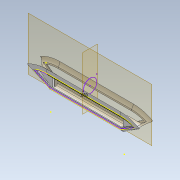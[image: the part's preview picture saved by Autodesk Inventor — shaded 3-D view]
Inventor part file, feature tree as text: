
AUTODESK INVENTOR PART (.ipt)
format: ipt  version: 2021 (Build 250183000, 183)  size: 614,912 bytes
history: native  units: in
note: dims shown in document units (in); Inventor stores cm internally (conversion verified against a paired STEP export)
features: sketch x11, extrude x7, move_body x4, plane x3, fillet x3, sweep x2, direct_edit x2, mirror x2, shell x1, projected_geometry x1
ambient origin geometry x8: Origin, YZ Plane, XZ Plane, XY Plane, X Axis, Y Axis, Z Axis, Center Point
bodies: Solid1 (feature_tree)
feature tree (36):
  extrude  "Extrusion1"  Depth=1.0in
  sweep  "Sweep1"
  direct_edit  "Direct Edit1"
  plane  "Work Plane1"
  plane  "Work Plane2"
  sweep  "Sweep2"
  fillet  "Fillet1"  [1 undecoded]
  fillet  "Fillet2"  Radius=2.75in
  fillet  "Fillet3"  [1 undecoded]
  shell  "Shell1"  Thickness=0.19in
  sketch  "Sketch4"  dims[d10=0.0in d11=0.0in d12=0.375in]
  extrude  "Extrusion2"  Depth=0.05in
  extrude  "Extrusion3"  Depth=0.05in TaperAngle=0.0deg
  plane  "Work Plane3"
  extrude  "Extrusion5"  Depth=0.7068in
  mirror  "Mirror2"
  extrude  "Extrusion6"  Depth=0.05in
  extrude  "Extrusion7"  Depth=0.7068in TaperAngle=0.0deg
  extrude  "Extrusion8"  Depth=0.31in TaperAngle=0.0deg
  mirror  "Mirror3"
  sketch  "Sketch10"  dims[d35=0.05in d36=0.0in d37=0.05in d38=0.0in d42=0.5in d43=0.05in d44=0.08in d45=0.0in d46=0.31in d47=0.0in d48=0.12in d49=0.7068in d50=0.0in d51=0.12in d52=0.035in d53=0.035in d54=0.7068in d55=0.0in d56=0.0in d57=0.0in d58=-0.07in d59=0.0in d60=0.0in d61=-0.07in]
  direct_edit  "Direct Edit2"
  sketch  "Sketch1"  dims[d0=5.5in d1=1.0in]
  sketch  "Sketch2"  dims[d3=1.0in d4=1.0in]
  sketch  "3D Sketch1"
  sketch  "Sketch3"  dims[d5=1.0in d6=0.0in d7=0.5in d8=0.0in d9=0.0in]
  sketch  "3D Sketch2"
  sketch  "Sketch6"  dims[d13=0.0in d14=0.0in d15=0.375in d16=2.75in d17=0.5in d18=0.0in d19=0.0in]
  projected_geometry  "Projected Loop2"
  sketch  "Sketch7"  dims[d20=0.2in d21=0.2in d22=0.2in d23=0.03in d24=0.03in d25=0.2in]
  sketch  "Sketch8"  dims[d26=0.2in d27=0.2in d28=0.2in d29=0.03in d30=0.03in d31=0.2in d32=0.19in]
  sketch  "Sketch9"  dims[d33=0.1in d34=0.05in]
  move_body  "Move1"
  move_body  "Move2"
  move_body  "Move3"
  move_body  "Move4"
note: 2 required parameter values undecoded (feature->parameter linkage not recoverable at this tier; creation-order binding heuristic only, values carry confidence <= 0.55)
